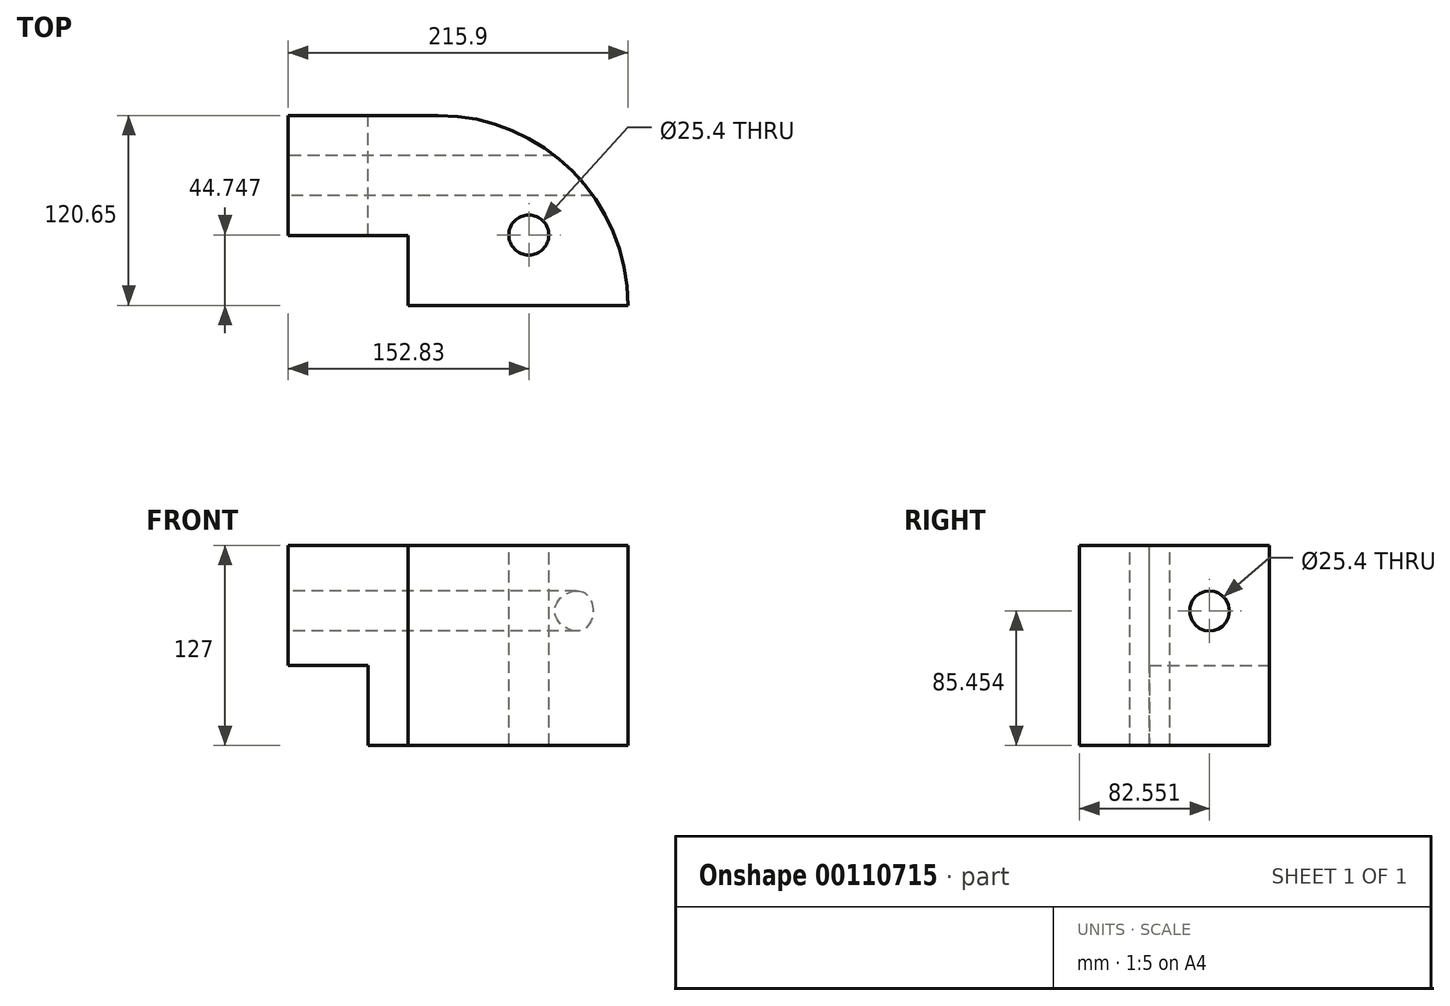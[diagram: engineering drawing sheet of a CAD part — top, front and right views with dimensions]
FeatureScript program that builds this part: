
annotation { "Feature Type Name" : "Feature", "Feature Type Description" : "" }
export const myFeature = defineFeature(function(context is Context, id is Id, definition is map)
    precondition{}
    {
        {
            var Q0;
            Q0=qCreatedBy(makeId("Top.planeOp"),FACE);
            var sketch = newSketch(context, id + "F0", { "sketchPlane" : qUnion([Q0])});
            skLineSegment(sketch, "E0.bottom", {"start": v(-150.87, 85.1) * mm, "end": v(65.03, 85.1) * mm});
            skLineSegment(sketch, "E0.top", {"start": v(-150.87, -35.55) * mm, "end": v(65.03, -35.55) * mm});
            skLineSegment(sketch, "E0.left", {"start": v(-150.87, 85.1) * mm, "end": v(-150.87, -35.55) * mm});
            skLineSegment(sketch, "E0.right", {"start": v(65.03, 85.1) * mm, "end": v(65.03, -35.55) * mm});
            skSolve(sketch);
        }
        {
            var Q0;
            Q0=makeQuery(id+"F0.imprint","IMPRINT",FACE,{"disambiguationData":[TD([[makeQuery(id+"F0.imprint","IMPRINT",EDGE,{"derivedFrom":sQuery(id+"F0.wireOp",EDGE,"E0.bottom")}),-1.0]])]});
            extrude(context, id + "F1", {"entities" : qUnion([Q0]), "depth" : 127 * mm});
        }
        {
            var Q0;
            Q0=makeQuery(id+"F1.opExtrude","CAP_FACE",FACE,{"disambiguationData":[OSD([sQuery(id+"F0.wireOp",EDGE,"E0.bottom"),sQuery(id+"F0.wireOp",EDGE,"E0.top"),sQuery(id+"F0.wireOp",EDGE,"E0.left"),sQuery(id+"F0.wireOp",EDGE,"E0.right")])],"isStart":false});
            var sketch = newSketch(context, id + "F2", { "sketchPlane" : qUnion([Q0])});
            skLineSegment(sketch, "E1.bottom", {"start": v(-150.87, -35.55) * mm, "end": v(-74.67, -35.55) * mm});
            skLineSegment(sketch, "E1.top", {"start": v(-150.87, 8.9) * mm, "end": v(-74.67, 8.9) * mm});
            skLineSegment(sketch, "E1.left", {"start": v(-150.87, -35.55) * mm, "end": v(-150.87, 8.9) * mm});
            skLineSegment(sketch, "E1.right", {"start": v(-74.67, -35.55) * mm, "end": v(-74.67, 8.9) * mm});
            skSolve(sketch);
        }
        {
            var Q0;
            Q0=makeQuery(id+"F2.imprint","IMPRINT",FACE,{"disambiguationData":[TD([[makeQuery(id+"F2.imprint","IMPRINT",EDGE,{"derivedFrom":sQuery(id+"F2.wireOp",EDGE,"E1.bottom")}),1.0]])]});
            extrude(context, id + "F3", {"entities" : qUnion([Q0]), "operationType" : NewBodyOperationType.REMOVE, "oppositeDirection" : true, "depth" : 25.4 * mm});
        }
        {
            var Q0;
            Q0=makeQuery(id+"F3.boolean.opBoolean","COPY",FACE,{"derivedFrom":makeQuery(id+"F3.opExtrude","CAP_FACE",FACE,{"disambiguationData":[OSD([sQuery(id+"F2.wireOp",EDGE,"E1.bottom"),sQuery(id+"F2.wireOp",EDGE,"E1.top"),sQuery(id+"F2.wireOp",EDGE,"E1.left"),sQuery(id+"F2.wireOp",EDGE,"E1.right")])],"isStart":false})});
            extrude(context, id + "F4", {"entities" : qUnion([Q0]), "operationType" : NewBodyOperationType.REMOVE, "endBound" : BoundingType.THROUGH_ALL, "oppositeDirection" : true, "depth" : 25.4 * mm});
        }
        {
            var Q0;
            Q0=makeQuery(id+"F1.opExtrude","CAP_FACE",FACE,{"disambiguationData":[OSD([sQuery(id+"F0.wireOp",EDGE,"E0.bottom"),sQuery(id+"F0.wireOp",EDGE,"E0.top"),sQuery(id+"F0.wireOp",EDGE,"E0.left"),sQuery(id+"F0.wireOp",EDGE,"E0.right")])],"isStart":false});
            var sketch = newSketch(context, id + "F5", { "sketchPlane" : qUnion([Q0])});
            skArc(sketch, "E2", {"start": v(65.03, -35.55) * mm, "mid": v(29.69, 49.76) * mm, "end": v(-55.62, 85.1) * mm});
            skSolve(sketch);
        }
        {
            var Q0;
            {var subQ0=sQuery(id+"F5.wireOp",EDGE,"E2");Q0=makeQuery(id+"F5.imprint","IMPRINT",FACE,{"disambiguationData":[TD([[makeQuery(id+"F5.imprint","IMPRINT",EDGE,{"derivedFrom":subQ0}),-1.0]])]});}
            extrude(context, id + "F6", {"entities" : qUnion([Q0]), "operationType" : NewBodyOperationType.REMOVE, "endBound" : BoundingType.THROUGH_ALL, "oppositeDirection" : true, "depth" : 25.4 * mm});
        }
        {
            var Q0;
            Q0=makeQuery(id+"F1.opExtrude","SWEPT_FACE",FACE,{"disambiguationData":[OSD([sQuery(id+"F0.wireOp",EDGE,"E0.bottom")])]});
            var sketch = newSketch(context, id + "F7", { "sketchPlane" : qUnion([Q0])});
            skLineSegment(sketch, "E3.bottom", {"start": v(150.87, 0) * mm, "end": v(100.07, 0) * mm});
            skLineSegment(sketch, "E3.top", {"start": v(150.87, 50.8) * mm, "end": v(100.07, 50.8) * mm});
            skLineSegment(sketch, "E3.left", {"start": v(150.87, 0) * mm, "end": v(150.87, 50.8) * mm});
            skLineSegment(sketch, "E3.right", {"start": v(100.07, 0) * mm, "end": v(100.07, 50.8) * mm});
            skSolve(sketch);
        }
        {
            var Q0;
            Q0=makeQuery(id+"F7.imprint","IMPRINT",FACE,{"disambiguationData":[TD([[makeQuery(id+"F7.imprint","IMPRINT",EDGE,{"derivedFrom":sQuery(id+"F7.wireOp",EDGE,"E3.bottom")}),-1.0]])]});
            extrude(context, id + "F8", {"entities" : qUnion([Q0]), "operationType" : NewBodyOperationType.REMOVE, "endBound" : BoundingType.THROUGH_ALL, "oppositeDirection" : true, "depth" : 25.4 * mm});
        }
        {
            var Q0;
            Q0=makeQuery(id+"F1.opExtrude","SWEPT_FACE",FACE,{"disambiguationData":[OSD([sQuery(id+"F0.wireOp",EDGE,"E0.left")])]});
            var sketch = newSketch(context, id + "F9", { "sketchPlane" : qUnion([Q0])});
            skCircle(sketch, "E4", {"center": v(-47, 85.45) * mm, "radius": 12.7 * mm});
            skPoint(sketch, "E4.centerSnap0", {"position": v(-47, 50.8) * mm});
            skSolve(sketch);
        }
        {
            var Q0;
            Q0=makeQuery(id+"F9.imprint","IMPRINT",FACE,{"disambiguationData":[TD([[makeQuery(id+"F9.imprint","IMPRINT",EDGE,{"derivedFrom":sQuery(id+"F9.wireOp",EDGE,"E4")}),1.0]])]});
            extrude(context, id + "F10", {"entities" : qUnion([Q0]), "operationType" : NewBodyOperationType.REMOVE, "endBound" : BoundingType.THROUGH_ALL, "oppositeDirection" : true, "depth" : 25.4 * mm});
        }
        {
            var Q0;
            Q0=makeQuery(id+"F1.opExtrude","CAP_FACE",FACE,{"disambiguationData":[OSD([sQuery(id+"F0.wireOp",EDGE,"E0.bottom"),sQuery(id+"F0.wireOp",EDGE,"E0.top"),sQuery(id+"F0.wireOp",EDGE,"E0.left"),sQuery(id+"F0.wireOp",EDGE,"E0.right")])],"isStart":false});
            var sketch = newSketch(context, id + "F11", { "sketchPlane" : qUnion([Q0])});
            skLineSegment(sketch, "E5.bottom", {"start": v(65.03, -35.55) * mm, "end": v(1.53, -35.55) * mm});
            skLineSegment(sketch, "E5.top", {"start": v(65.03, 8.9) * mm, "end": v(1.53, 8.9) * mm});
            skLineSegment(sketch, "E5.left", {"start": v(65.03, -35.55) * mm, "end": v(65.03, 8.9) * mm});
            skLineSegment(sketch, "E5.right", {"start": v(1.53, -35.55) * mm, "end": v(1.53, 8.9) * mm});
            skSolve(sketch);
        }
        {
            var Q0;
            {var subQ1=sQuery(id+"F11.wireOp",EDGE,"E5.right");Q0=makeQuery(id+"F11.imprint","IMPRINT",FACE,{"disambiguationData":[TD([[makeQuery(id+"F11.imprint","IMPRINT",EDGE,{"derivedFrom":subQ1}),1.0]])]});}
            var sketch = newSketch(context, id + "F12", { "sketchPlane" : qUnion([Q0])});
            skCircle(sketch, "E6", {"center": v(1.96, 9.2) * mm, "radius": 12.7 * mm});
            skSolve(sketch);
        }
        {
            var Q0;
            Q0=qSketchRegion(id+"F12",true);
            extrude(context, id + "F13", {"entities" : qUnion([Q0]), "operationType" : NewBodyOperationType.REMOVE, "endBound" : BoundingType.THROUGH_ALL, "oppositeDirection" : true, "depth" : 25.4 * mm});
        }
    });
